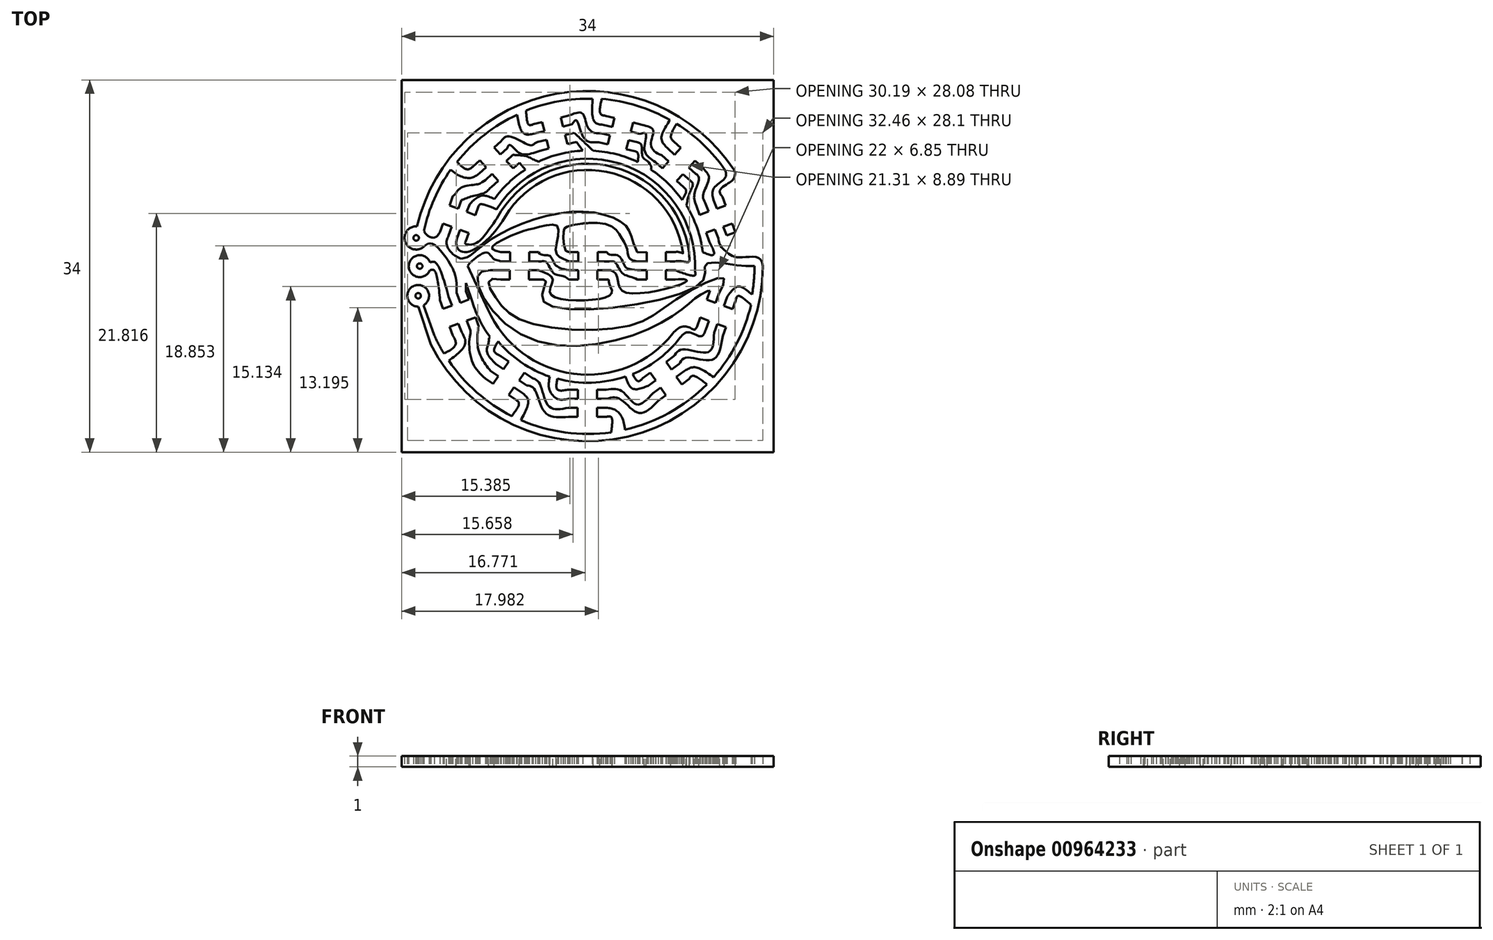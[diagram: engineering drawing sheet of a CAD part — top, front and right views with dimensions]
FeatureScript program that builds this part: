
annotation { "Feature Type Name" : "Feature", "Feature Type Description" : "" }
export const myFeature = defineFeature(function(context is Context, id is Id, definition is map)
    precondition{}
    {
        {
            var Q0;
            Q0=qCreatedBy(makeId("Top.planeOp"),FACE);
            var sketch = newSketch(context, id + "F0", { "sketchPlane" : qUnion([Q0])});
            skLineSegment(sketch, "E0", {"start": v(-17.5, -17.5) * mm, "end": v(17.5, -17.5) * mm});
            skLineSegment(sketch, "E1", {"start": v(17.5, -17.5) * mm, "end": v(17.5, 17.5) * mm});
            skLineSegment(sketch, "E2", {"start": v(17.5, 17.5) * mm, "end": v(-17.5, 17.5) * mm});
            skLineSegment(sketch, "E3", {"start": v(-17.5, 17.5) * mm, "end": v(-17.5, -17.5) * mm});
            skLineSegment(sketch, "E4", {"start": v(7.16, -11.8) * mm, "end": v(6.46, -12.3) * mm});
            skLineSegment(sketch, "E5", {"start": v(5.97, -11.6) * mm, "end": v(6.67, -11.1) * mm});
            skLineSegment(sketch, "E6", {"start": v(6.67, -11.1) * mm, "end": v(7.16, -11.8) * mm});
            skLineSegment(sketch, "E7", {"start": v(6.22, -10.44) * mm, "end": v(5.52, -10.93) * mm});
            skLineSegment(sketch, "E8", {"start": v(5.03, -10.23) * mm, "end": v(5.73, -9.75) * mm});
            skLineSegment(sketch, "E9", {"start": v(5.73, -9.75) * mm, "end": v(6.22, -10.44) * mm});
            skLineSegment(sketch, "E10", {"start": v(8.35, -8.95) * mm, "end": v(7.65, -9.44) * mm});
            skLineSegment(sketch, "E11", {"start": v(7.65, -9.44) * mm, "end": v(7.16, -8.74) * mm});
            skLineSegment(sketch, "E12", {"start": v(7.16, -8.74) * mm, "end": v(7.86, -8.26) * mm});
            skLineSegment(sketch, "E13", {"start": v(9.29, -10.31) * mm, "end": v(8.59, -10.8) * mm});
            skLineSegment(sketch, "E14", {"start": v(8.59, -10.8) * mm, "end": v(8.1, -10.1) * mm});
            skLineSegment(sketch, "E15", {"start": v(8.1, -10.1) * mm, "end": v(8.8, -9.62) * mm});
            skLineSegment(sketch, "E16", {"start": v(-10.85, 3.02) * mm, "end": v(-11.14, 2.22) * mm});
            skLineSegment(sketch, "E17", {"start": v(-11.94, 2.51) * mm, "end": v(-11.65, 3.31) * mm});
            skLineSegment(sketch, "E18", {"start": v(-11.65, 3.31) * mm, "end": v(-10.85, 3.02) * mm});
            skLineSegment(sketch, "E19", {"start": v(-12.4, 3.6) * mm, "end": v(-12.7, 2.8) * mm});
            skLineSegment(sketch, "E20", {"start": v(-13.5, 3.09) * mm, "end": v(-13.2, 3.89) * mm});
            skLineSegment(sketch, "E21", {"start": v(-13.2, 3.89) * mm, "end": v(-12.4, 3.6) * mm});
            skLineSegment(sketch, "E22", {"start": v(-11.51, 6.04) * mm, "end": v(-11.8, 5.24) * mm});
            skLineSegment(sketch, "E23", {"start": v(-11.8, 5.24) * mm, "end": v(-12.6, 5.53) * mm});
            skLineSegment(sketch, "E24", {"start": v(-12.6, 5.53) * mm, "end": v(-12.31, 6.38) * mm});
            skLineSegment(sketch, "E25", {"start": v(-9.96, 5.46) * mm, "end": v(-10.25, 4.66) * mm});
            skLineSegment(sketch, "E26", {"start": v(-10.25, 4.66) * mm, "end": v(-11.05, 4.96) * mm});
            skLineSegment(sketch, "E27", {"start": v(-11.05, 4.96) * mm, "end": v(-10.76, 5.65) * mm});
            skLineSegment(sketch, "E28", {"start": v(1.83, 11.11) * mm, "end": v(1, 11.32) * mm});
            skLineSegment(sketch, "E29", {"start": v(1.21, 12.14) * mm, "end": v(2.04, 11.94) * mm});
            skLineSegment(sketch, "E30", {"start": v(2.04, 11.94) * mm, "end": v(1.83, 11.11) * mm});
            skLineSegment(sketch, "E31", {"start": v(2.24, 12.71) * mm, "end": v(1.42, 12.92) * mm});
            skLineSegment(sketch, "E32", {"start": v(1.63, 13.74) * mm, "end": v(2.45, 13.54) * mm});
            skLineSegment(sketch, "E33", {"start": v(2.45, 13.54) * mm, "end": v(2.24, 12.71) * mm});
            skLineSegment(sketch, "E34", {"start": v(4.77, 12.09) * mm, "end": v(3.94, 12.3) * mm});
            skLineSegment(sketch, "E35", {"start": v(3.94, 12.3) * mm, "end": v(4.15, 13.12) * mm});
            skLineSegment(sketch, "E36", {"start": v(4.15, 13.12) * mm, "end": v(4.97, 12.9) * mm});
            skLineSegment(sketch, "E37", {"start": v(4.36, 10.48) * mm, "end": v(3.53, 10.69) * mm});
            skLineSegment(sketch, "E38", {"start": v(3.53, 10.69) * mm, "end": v(3.74, 11.51) * mm});
            skLineSegment(sketch, "E39", {"start": v(3.74, 11.51) * mm, "end": v(4.56, 11.3) * mm});
            skLineSegment(sketch, "E40", {"start": v(-2.45, 13.58) * mm, "end": v(-1.63, 13.8) * mm});
            skLineSegment(sketch, "E41", {"start": v(-1.42, 12.97) * mm, "end": v(-2.24, 12.76) * mm});
            skLineSegment(sketch, "E42", {"start": v(-2.24, 12.76) * mm, "end": v(-2.45, 13.58) * mm});
            skLineSegment(sketch, "E43", {"start": v(-2.06, 11.98) * mm, "end": v(-1.24, 12.18) * mm});
            skLineSegment(sketch, "E44", {"start": v(-1.03, 11.36) * mm, "end": v(-1.86, 11.15) * mm});
            skLineSegment(sketch, "E45", {"start": v(-1.86, 11.15) * mm, "end": v(-2.06, 11.98) * mm});
            skLineSegment(sketch, "E46", {"start": v(-4.58, 11.35) * mm, "end": v(-3.76, 11.55) * mm});
            skLineSegment(sketch, "E47", {"start": v(-3.76, 11.55) * mm, "end": v(-3.55, 10.73) * mm});
            skLineSegment(sketch, "E48", {"start": v(-3.55, 10.73) * mm, "end": v(-4.38, 10.52) * mm});
            skLineSegment(sketch, "E49", {"start": v(-4.97, 12.96) * mm, "end": v(-4.15, 13.16) * mm});
            skLineSegment(sketch, "E50", {"start": v(-4.15, 13.16) * mm, "end": v(-3.94, 12.34) * mm});
            skLineSegment(sketch, "E51", {"start": v(-3.94, 12.34) * mm, "end": v(-4.77, 12.13) * mm});
            skLineSegment(sketch, "E52", {"start": v(-8.54, 10.84) * mm, "end": v(-7.9, 11.41) * mm});
            skLineSegment(sketch, "E53", {"start": v(-7.34, 10.78) * mm, "end": v(-7.97, 10.21) * mm});
            skLineSegment(sketch, "E54", {"start": v(-7.97, 10.21) * mm, "end": v(-8.54, 10.84) * mm});
            skLineSegment(sketch, "E55", {"start": v(-7.44, 9.6) * mm, "end": v(-6.81, 10.18) * mm});
            skLineSegment(sketch, "E56", {"start": v(-6.22, 9.45) * mm, "end": v(-6.8, 8.94) * mm});
            skLineSegment(sketch, "E57", {"start": v(-6.8, 8.94) * mm, "end": v(-7.44, 9.6) * mm});
            skLineSegment(sketch, "E58", {"start": v(-9.34, 7.87) * mm, "end": v(-8.74, 8.44) * mm});
            skLineSegment(sketch, "E59", {"start": v(-8.74, 8.44) * mm, "end": v(-8.17, 7.8) * mm});
            skLineSegment(sketch, "E60", {"start": v(-8.17, 7.8) * mm, "end": v(-8.8, 7.24) * mm});
            skLineSegment(sketch, "E61", {"start": v(-10.47, 9.1) * mm, "end": v(-9.84, 9.67) * mm});
            skLineSegment(sketch, "E62", {"start": v(-9.84, 9.67) * mm, "end": v(-9.27, 9.04) * mm});
            skLineSegment(sketch, "E63", {"start": v(-9.27, 9.04) * mm, "end": v(-9.9, 8.47) * mm});
            skLineSegment(sketch, "E64", {"start": v(6.84, 8.95) * mm, "end": v(6.2, 9.52) * mm});
            skLineSegment(sketch, "E65", {"start": v(6.77, 10.15) * mm, "end": v(7.4, 9.58) * mm});
            skLineSegment(sketch, "E66", {"start": v(7.4, 9.58) * mm, "end": v(6.84, 8.95) * mm});
            skLineSegment(sketch, "E67", {"start": v(7.95, 10.17) * mm, "end": v(7.32, 10.74) * mm});
            skLineSegment(sketch, "E68", {"start": v(7.89, 11.37) * mm, "end": v(8.52, 10.8) * mm});
            skLineSegment(sketch, "E69", {"start": v(8.52, 10.8) * mm, "end": v(7.95, 10.17) * mm});
            skLineSegment(sketch, "E70", {"start": v(9.88, 8.43) * mm, "end": v(9.25, 9) * mm});
            skLineSegment(sketch, "E71", {"start": v(9.25, 9) * mm, "end": v(9.82, 9.63) * mm});
            skLineSegment(sketch, "E72", {"start": v(9.82, 9.63) * mm, "end": v(10.45, 9.06) * mm});
            skLineSegment(sketch, "E73", {"start": v(8.77, 7.21) * mm, "end": v(8.14, 7.78) * mm});
            skLineSegment(sketch, "E74", {"start": v(8.14, 7.78) * mm, "end": v(8.7, 8.41) * mm});
            skLineSegment(sketch, "E75", {"start": v(8.7, 8.41) * mm, "end": v(9.34, 7.84) * mm});
            skLineSegment(sketch, "E76", {"start": v(10.24, 4.7) * mm, "end": v(9.95, 5.5) * mm});
            skLineSegment(sketch, "E77", {"start": v(10.75, 5.78) * mm, "end": v(11.04, 4.98) * mm});
            skLineSegment(sketch, "E78", {"start": v(11.04, 4.98) * mm, "end": v(10.24, 4.7) * mm});
            skLineSegment(sketch, "E79", {"start": v(11.8, 5.25) * mm, "end": v(11.5, 6.05) * mm});
            skLineSegment(sketch, "E80", {"start": v(12.3, 6.34) * mm, "end": v(12.6, 5.54) * mm});
            skLineSegment(sketch, "E81", {"start": v(12.6, 5.54) * mm, "end": v(11.8, 5.25) * mm});
            skLineSegment(sketch, "E82", {"start": v(12.68, 2.8) * mm, "end": v(12.4, 3.6) * mm});
            skLineSegment(sketch, "E83", {"start": v(12.4, 3.6) * mm, "end": v(13.2, 3.9) * mm});
            skLineSegment(sketch, "E84", {"start": v(13.2, 3.9) * mm, "end": v(13.48, 3.1) * mm});
            skLineSegment(sketch, "E85", {"start": v(13.48, 3.1) * mm, "end": v(12.68, 2.8) * mm});
            skLineSegment(sketch, "E86", {"start": v(11.13, 2.25) * mm, "end": v(10.84, 3.05) * mm});
            skLineSegment(sketch, "E87", {"start": v(10.84, 3.05) * mm, "end": v(11.64, 3.34) * mm});
            skLineSegment(sketch, "E88", {"start": v(11.64, 3.34) * mm, "end": v(11.93, 2.54) * mm});
            skLineSegment(sketch, "E89", {"start": v(12.63, -5.57) * mm, "end": v(12.34, -6.36) * mm});
            skLineSegment(sketch, "E90", {"start": v(11.54, -6.07) * mm, "end": v(11.83, -5.27) * mm});
            skLineSegment(sketch, "E91", {"start": v(11.83, -5.27) * mm, "end": v(12.63, -5.57) * mm});
            skLineSegment(sketch, "E92", {"start": v(11.08, -4.99) * mm, "end": v(10.8, -5.79) * mm});
            skLineSegment(sketch, "E93", {"start": v(10, -5.5) * mm, "end": v(10.28, -4.7) * mm});
            skLineSegment(sketch, "E94", {"start": v(10.28, -4.7) * mm, "end": v(11.08, -4.99) * mm});
            skLineSegment(sketch, "E95", {"start": v(11.97, -2.55) * mm, "end": v(11.68, -3.34) * mm});
            skLineSegment(sketch, "E96", {"start": v(11.68, -3.34) * mm, "end": v(10.88, -3.05) * mm});
            skLineSegment(sketch, "E97", {"start": v(10.88, -3.05) * mm, "end": v(11.17, -2.26) * mm});
            skLineSegment(sketch, "E98", {"start": v(13.52, -3.12) * mm, "end": v(13.23, -3.92) * mm});
            skLineSegment(sketch, "E99", {"start": v(13.23, -3.92) * mm, "end": v(12.43, -3.63) * mm});
            skLineSegment(sketch, "E100", {"start": v(12.43, -3.63) * mm, "end": v(12.72, -2.83) * mm});
            skLineSegment(sketch, "E101", {"start": v(-0.9, -13.78) * mm, "end": v(-1.75, -13.78) * mm});
            skLineSegment(sketch, "E102", {"start": v(-1.75, -12.93) * mm, "end": v(-0.9, -12.93) * mm});
            skLineSegment(sketch, "E103", {"start": v(-0.9, -12.93) * mm, "end": v(-0.9, -13.78) * mm});
            skLineSegment(sketch, "E104", {"start": v(-0.9, -12.12) * mm, "end": v(-1.74, -12.12) * mm});
            skLineSegment(sketch, "E105", {"start": v(-1.74, -11.27) * mm, "end": v(-0.9, -11.27) * mm});
            skLineSegment(sketch, "E106", {"start": v(-0.9, -11.27) * mm, "end": v(-0.9, -12.12) * mm});
            skLineSegment(sketch, "E107", {"start": v(1.7, -12.12) * mm, "end": v(0.86, -12.12) * mm});
            skLineSegment(sketch, "E108", {"start": v(0.86, -12.12) * mm, "end": v(0.86, -11.27) * mm});
            skLineSegment(sketch, "E109", {"start": v(0.86, -11.27) * mm, "end": v(1.7, -11.27) * mm});
            skLineSegment(sketch, "E110", {"start": v(1.7, -13.78) * mm, "end": v(0.85, -13.78) * mm});
            skLineSegment(sketch, "E111", {"start": v(0.85, -13.78) * mm, "end": v(0.85, -12.93) * mm});
            skLineSegment(sketch, "E112", {"start": v(0.85, -12.93) * mm, "end": v(1.7, -12.93) * mm});
            skLineSegment(sketch, "E113", {"start": v(-8.65, -10.76) * mm, "end": v(-9.34, -10.27) * mm});
            skLineSegment(sketch, "E114", {"start": v(-8.85, -9.58) * mm, "end": v(-8.16, -10.07) * mm});
            skLineSegment(sketch, "E115", {"start": v(-8.16, -10.07) * mm, "end": v(-8.65, -10.76) * mm});
            skLineSegment(sketch, "E116", {"start": v(-7.69, -9.41) * mm, "end": v(-8.38, -8.93) * mm});
            skLineSegment(sketch, "E117", {"start": v(-7.9, -8.23) * mm, "end": v(-7.2, -8.72) * mm});
            skLineSegment(sketch, "E118", {"start": v(-7.2, -8.72) * mm, "end": v(-7.69, -9.41) * mm});
            skLineSegment(sketch, "E119", {"start": v(-5.56, -10.9) * mm, "end": v(-6.25, -10.42) * mm});
            skLineSegment(sketch, "E120", {"start": v(-6.25, -10.42) * mm, "end": v(-5.77, -9.72) * mm});
            skLineSegment(sketch, "E121", {"start": v(-5.77, -9.72) * mm, "end": v(-5.07, -10.2) * mm});
            skLineSegment(sketch, "E122", {"start": v(-6.52, -12.25) * mm, "end": v(-7.21, -11.77) * mm});
            skLineSegment(sketch, "E123", {"start": v(-7.21, -11.77) * mm, "end": v(-6.72, -11.07) * mm});
            skLineSegment(sketch, "E124", {"start": v(-6.72, -11.07) * mm, "end": v(-6.03, -11.56) * mm});
            skLineSegment(sketch, "E125", {"start": v(-10.24, -4.7) * mm, "end": v(-9.96, -5.45) * mm});
            skLineSegment(sketch, "E126", {"start": v(-10.75, -5.78) * mm, "end": v(-11.04, -4.98) * mm});
            skLineSegment(sketch, "E127", {"start": v(-11.04, -4.98) * mm, "end": v(-10.24, -4.7) * mm});
            skLineSegment(sketch, "E128", {"start": v(-11.8, -5.25) * mm, "end": v(-11.5, -6.05) * mm});
            skLineSegment(sketch, "E129", {"start": v(-12.3, -6.34) * mm, "end": v(-12.6, -5.54) * mm});
            skLineSegment(sketch, "E130", {"start": v(-12.6, -5.54) * mm, "end": v(-11.8, -5.25) * mm});
            skLineSegment(sketch, "E131", {"start": v(-12.68, -2.8) * mm, "end": v(-12.4, -3.6) * mm});
            skLineSegment(sketch, "E132", {"start": v(-12.4, -3.6) * mm, "end": v(-13.2, -3.9) * mm});
            skLineSegment(sketch, "E133", {"start": v(-13.2, -3.9) * mm, "end": v(-13.48, -3.1) * mm});
            skLineSegment(sketch, "E134", {"start": v(-11.1, -2.3) * mm, "end": v(-10.84, -3.05) * mm});
            skLineSegment(sketch, "E135", {"start": v(-10.84, -3.05) * mm, "end": v(-11.64, -3.34) * mm});
            skLineSegment(sketch, "E136", {"start": v(-11.64, -3.34) * mm, "end": v(-11.96, -2.44) * mm});
            skLineSegment(sketch, "E137", {"start": v(0.9, 1.27) * mm, "end": v(1.76, 1.27) * mm});
            skLineSegment(sketch, "E138", {"start": v(1.76, 0.42) * mm, "end": v(0.9, 0.42) * mm});
            skLineSegment(sketch, "E139", {"start": v(0.9, 0.42) * mm, "end": v(0.9, 1.27) * mm});
            skLineSegment(sketch, "E140", {"start": v(0.9, -0.38) * mm, "end": v(1.75, -0.38) * mm});
            skLineSegment(sketch, "E141", {"start": v(1.75, -1.23) * mm, "end": v(0.9, -1.23) * mm});
            skLineSegment(sketch, "E142", {"start": v(0.9, -1.23) * mm, "end": v(0.9, -0.38) * mm});
            skLineSegment(sketch, "E143", {"start": v(-1.7, -0.38) * mm, "end": v(-0.85, -0.38) * mm});
            skLineSegment(sketch, "E144", {"start": v(-0.85, -0.38) * mm, "end": v(-0.85, -1.23) * mm});
            skLineSegment(sketch, "E145", {"start": v(-0.85, -1.23) * mm, "end": v(-1.7, -1.23) * mm});
            skLineSegment(sketch, "E146", {"start": v(-1.7, 1.27) * mm, "end": v(-0.84, 1.27) * mm});
            skLineSegment(sketch, "E147", {"start": v(-0.84, 1.27) * mm, "end": v(-0.84, 0.42) * mm});
            skLineSegment(sketch, "E148", {"start": v(-0.84, 0.42) * mm, "end": v(-1.7, 0.42) * mm});
            skLineSegment(sketch, "E149", {"start": v(-5.34, 1.27) * mm, "end": v(-4.5, 1.27) * mm});
            skLineSegment(sketch, "E150", {"start": v(-4.5, 0.42) * mm, "end": v(-5.34, 0.42) * mm});
            skLineSegment(sketch, "E151", {"start": v(-5.34, 0.42) * mm, "end": v(-5.34, 1.27) * mm});
            skLineSegment(sketch, "E152", {"start": v(-5.35, -0.38) * mm, "end": v(-4.5, -0.38) * mm});
            skLineSegment(sketch, "E153", {"start": v(-4.5, -1.23) * mm, "end": v(-5.35, -1.23) * mm});
            skLineSegment(sketch, "E154", {"start": v(-5.35, -1.23) * mm, "end": v(-5.35, -0.38) * mm});
            skLineSegment(sketch, "E155", {"start": v(-7.94, -0.38) * mm, "end": v(-7.1, -0.38) * mm});
            skLineSegment(sketch, "E156", {"start": v(-7.1, -0.38) * mm, "end": v(-7.1, -1.23) * mm});
            skLineSegment(sketch, "E157", {"start": v(-7.1, -1.23) * mm, "end": v(-7.95, -1.23) * mm});
            skLineSegment(sketch, "E158", {"start": v(-7.94, 1.27) * mm, "end": v(-7.1, 1.27) * mm});
            skLineSegment(sketch, "E159", {"start": v(-7.1, 1.27) * mm, "end": v(-7.1, 0.42) * mm});
            skLineSegment(sketch, "E160", {"start": v(-7.1, 0.42) * mm, "end": v(-7.94, 0.42) * mm});
            skLineSegment(sketch, "E161", {"start": v(7.16, 1.27) * mm, "end": v(8, 1.27) * mm});
            skLineSegment(sketch, "E162", {"start": v(8, 0.42) * mm, "end": v(7.16, 0.42) * mm});
            skLineSegment(sketch, "E163", {"start": v(7.16, 0.42) * mm, "end": v(7.16, 1.27) * mm});
            skLineSegment(sketch, "E164", {"start": v(7.15, -0.38) * mm, "end": v(8, -0.38) * mm});
            skLineSegment(sketch, "E165", {"start": v(8, -1.23) * mm, "end": v(7.15, -1.23) * mm});
            skLineSegment(sketch, "E166", {"start": v(7.15, -1.23) * mm, "end": v(7.15, -0.38) * mm});
            skLineSegment(sketch, "E167", {"start": v(4.55, -0.38) * mm, "end": v(5.4, -0.38) * mm});
            skLineSegment(sketch, "E168", {"start": v(5.4, -0.38) * mm, "end": v(5.4, -1.23) * mm});
            skLineSegment(sketch, "E169", {"start": v(5.4, -1.23) * mm, "end": v(4.55, -1.23) * mm});
            skLineSegment(sketch, "E170", {"start": v(4.54, 1.24) * mm, "end": v(5.4, 1.27) * mm});
            skLineSegment(sketch, "E171", {"start": v(5.4, 1.27) * mm, "end": v(5.4, 0.42) * mm});
            skLineSegment(sketch, "E172", {"start": v(5.4, 0.42) * mm, "end": v(4.56, 0.42) * mm});
            skFitSpline(sketch, "E173", {"points": [v(-4.5, 1.27) * mm, v(-3.5, 0.96) * mm, v(-3.03, 0.24) * mm, v(-1.7, -0.38) * mm], "startDerivative": vector(2.64, -3.87) * mm, "endDerivative": vector(5.84, -1.05) * mm});
            skFitSpline(sketch, "E174", {"points": [v(-4.5, 0.42) * mm, v(-3.8, 0.38) * mm, v(-3.1, -0.65) * mm, v(-1.7, -1.23) * mm], "startDerivative": vector(2.54, -0.29) * mm, "endDerivative": vector(4.22, -3.88) * mm});
            skFitSpline(sketch, "E175", {"points": [v(1.76, 1.27) * mm, v(2.76, 0.98) * mm, v(3.4, 0) * mm, v(4.55, -0.38) * mm], "startDerivative": vector(2.64, -3.87) * mm, "endDerivative": vector(6.94, -0.97) * mm});
            skFitSpline(sketch, "E176", {"points": [v(1.76, 0.42) * mm, v(2.45, 0.38) * mm, v(3.16, -0.64) * mm, v(4.55, -1.23) * mm], "startDerivative": vector(2.54, -0.29) * mm, "endDerivative": vector(3.98, -2.38) * mm});
            skCircle(sketch, "E177", {"center": v(-15.34, 0) * mm, "radius": 0.25 * mm});
            skArc(sketch, "E178", {"start": v(13.36, 8.8) * mm, "mid": v(-2.8, 15.75) * mm, "end": v(-15.58, 3.64) * mm});
            skArc(sketch, "E179", {"start": v(16, 0) * mm, "mid": v(3.67, -15.57) * mm, "end": v(-14.31, -7.15) * mm});
            skArc(sketch, "E180", {"start": v(-8.32, 5.2) * mm, "mid": v(2.93, 9.37) * mm, "end": v(9.8, -0.47) * mm});
            skArc(sketch, "E181", {"start": v(-8.5, 6.14) * mm, "mid": v(-7.22, 7.61) * mm, "end": v(-5.68, 8.82) * mm});
            skArc(sketch, "E182", {"start": v(-4.48, 9.55) * mm, "mid": v(-2.5, 10.25) * mm, "end": v(-0.44, 10.54) * mm});
            skArc(sketch, "E183", {"start": v(0.5, 10.54) * mm, "mid": v(2.6, 10.23) * mm, "end": v(4.58, 9.5) * mm});
            skArc(sketch, "E184", {"start": v(5.77, 8.82) * mm, "mid": v(7.33, 7.58) * mm, "end": v(8.63, 6.05) * mm});
            skArc(sketch, "E185", {"start": v(9.01, 5.55) * mm, "mid": v(10, 3.5) * mm, "end": v(10.5, 1.27) * mm});
            skArc(sketch, "E186", {"start": v(-14.95, 3.23) * mm, "mid": v(-14, 6.15) * mm, "end": v(-12.5, 8.82) * mm});
            skArc(sketch, "E187", {"start": v(-11.93, 9.5) * mm, "mid": v(-9.43, 12) * mm, "end": v(-6.43, 13.84) * mm});
            skArc(sketch, "E188", {"start": v(-5.62, 14.22) * mm, "mid": v(-2.64, 15.06) * mm, "end": v(0.46, 15.28) * mm});
            skArc(sketch, "E189", {"start": v(1.29, 15.28) * mm, "mid": v(4.51, 14.65) * mm, "end": v(7.53, 13.35) * mm});
            skArc(sketch, "E190", {"start": v(8.11, 13) * mm, "mid": v(10.56, 11.1) * mm, "end": v(12.58, 8.75) * mm});
            skFitSpline(sketch, "E191", {"points": [v(1.63, 13.74) * mm, v(1.18, 13.92) * mm, v(1.29, 15.28) * mm], "startDerivative": vector(-1.46, 0.16) * mm, "endDerivative": vector(0.6, 2.7) * mm});
            skFitSpline(sketch, "E192", {"points": [v(1.42, 12.92) * mm, v(0.64, 13.17) * mm, v(0.46, 15.28) * mm], "startDerivative": vector(-2.38, 0.13) * mm, "endDerivative": vector(0.25, 4.28) * mm});
            skFitSpline(sketch, "E193", {"points": [v(-4.97, 12.96) * mm, v(-5.37, 12.92) * mm, v(-5.62, 14.22) * mm], "startDerivative": vector(-1.25, -0.48) * mm, "endDerivative": vector(-0.15, 2.7) * mm});
            skFitSpline(sketch, "E194", {"points": [v(-4.77, 12.13) * mm, v(-5.84, 12.13) * mm, v(-6.43, 13.84) * mm], "startDerivative": vector(-2.78, -0.66) * mm, "endDerivative": vector(-0.64, 3.88) * mm});
            skFitSpline(sketch, "E195", {"points": [v(7.89, 11.37) * mm, v(7.6, 11.76) * mm, v(8.11, 13) * mm], "startDerivative": vector(-1.05, 0.86) * mm, "endDerivative": vector(1.3, 2.28) * mm});
            skFitSpline(sketch, "E196", {"points": [v(7.32, 10.74) * mm, v(6.74, 11.66) * mm, v(7.53, 13.35) * mm], "startDerivative": vector(-1.92, 1.95) * mm, "endDerivative": vector(2.16, 3.22) * mm});
            skFitSpline(sketch, "E197", {"points": [v(11.5, 6.05) * mm, v(11.5, 7.1) * mm, v(12.57, 8.1) * mm, v(12.58, 8.75) * mm], "startDerivative": vector(-0.86, 3.26) * mm, "endDerivative": vector(-0.7, 2.5) * mm});
            skFitSpline(sketch, "E198", {"points": [v(12.3, 6.34) * mm, v(12.08, 6.94) * mm, v(13.04, 7.7) * mm, v(13.35, 8.03) * mm, v(13.36, 8.8) * mm], "startDerivative": vector(-1.95, 2.73) * mm, "endDerivative": vector(-2.58, 3.05) * mm});
            skFitSpline(sketch, "E199", {"points": [v(-10.47, 9.1) * mm, v(-10.97, 8.84) * mm, v(-11.93, 9.5) * mm], "startDerivative": vector(-1.13, -1.02) * mm, "endDerivative": vector(-1.76, 1.66) * mm});
            skFitSpline(sketch, "E200", {"points": [v(-9.9, 8.47) * mm, v(-10.8, 8.05) * mm, v(-12.5, 8.82) * mm], "startDerivative": vector(-2, -1.6) * mm, "endDerivative": vector(-2.69, 2.72) * mm});
            skArc(sketch, "E201", {"start": v(-14.41, -0.38) * mm, "mid": v(-16.34, 0.02) * mm, "end": v(-14.4, 0.33) * mm});
            skFitSpline(sketch, "E202", {"points": [v(-12.31, 6.38) * mm, v(-11.61, 7.13) * mm, v(-10.14, 7.46) * mm, v(-9.34, 7.87) * mm], "startDerivative": vector(2.35, 1.53) * mm, "endDerivative": vector(4.22, 3) * mm});
            skFitSpline(sketch, "E203", {"points": [v(-11.51, 6.04) * mm, v(-10.56, 6.38) * mm, v(-9.34, 6.74) * mm, v(-8.8, 7.24) * mm], "startDerivative": vector(2.4, 0.9) * mm, "endDerivative": vector(1.63, 1.7) * mm});
            skFitSpline(sketch, "E204", {"points": [v(-7.9, 11.41) * mm, v(-7.29, 11.85) * mm, v(-5.98, 11.37) * mm, v(-5.18, 11.04) * mm, v(-4.58, 11.35) * mm], "startDerivative": vector(2.66, 3.35) * mm, "endDerivative": vector(2.59, 1.34) * mm});
            skFitSpline(sketch, "E205", {"points": [v(-7.34, 10.78) * mm, v(-7.13, 11.08) * mm, v(-6.38, 10.44) * mm, v(-5.7, 10.2) * mm, v(-4.38, 10.52) * mm], "startDerivative": vector(0.96, 2.67) * mm, "endDerivative": vector(4.46, 1.45) * mm});
            skFitSpline(sketch, "E206", {"points": [v(-1.63, 13.8) * mm, v(-0.47, 13.94) * mm, v(0, 12.7) * mm, v(1.21, 12.14) * mm], "startDerivative": vector(4.74, 1.94) * mm, "endDerivative": vector(5.2, 0.66) * mm});
            skFitSpline(sketch, "E207", {"points": [v(-1.42, 12.97) * mm, v(-1.02, 13.32) * mm, v(-0.6, 12.26) * mm, v(0, 11.41) * mm, v(1, 11.32) * mm], "startDerivative": vector(2.61, 4.43) * mm, "endDerivative": vector(4.4, 0.2) * mm});
            skFitSpline(sketch, "E208", {"points": [v(4.97, 12.9) * mm, v(5.97, 12.43) * mm, v(5.78, 11.12) * mm, v(6.77, 10.15) * mm], "startDerivative": vector(3.91, -0.95) * mm, "endDerivative": vector(4.74, -1.03) * mm});
            skFitSpline(sketch, "E209", {"points": [v(4.77, 12.09) * mm, v(5.32, 12.09) * mm, v(5.2, 10.58) * mm, v(6.2, 9.52) * mm], "startDerivative": vector(3.05, 0.85) * mm, "endDerivative": vector(3.66, -2.17) * mm});
            skFitSpline(sketch, "E210", {"points": [v(10.45, 9.06) * mm, v(11.08, 8.13) * mm, v(10.6, 6.74) * mm, v(10.75, 5.78) * mm], "startDerivative": vector(2.43, -3.28) * mm, "endDerivative": vector(2.43, -3.56) * mm});
            skFitSpline(sketch, "E211", {"points": [v(9.88, 8.43) * mm, v(10.16, 7.85) * mm, v(9.8, 6.82) * mm, v(9.95, 5.5) * mm], "startDerivative": vector(2.93, -1.68) * mm, "endDerivative": vector(1.97, -3.76) * mm});
            skFitSpline(sketch, "E212", {"points": [v(-6.81, 10.18) * mm, v(-5.65, 10.06) * mm, v(-4.48, 9.55) * mm], "startDerivative": vector(2, -0.4) * mm, "endDerivative": vector(2.64, -0.83) * mm});
            skFitSpline(sketch, "E213", {"points": [v(-1.24, 12.18) * mm, v(-0.5, 11.5) * mm, v(0.5, 10.54) * mm], "startDerivative": vector(1.55, -1.43) * mm, "endDerivative": vector(1.92, -1.85) * mm});
            skFitSpline(sketch, "E214", {"points": [v(-1.03, 11.36) * mm, v(-0.44, 10.54) * mm], "startDerivative": vector(0.6, -0.82) * mm, "endDerivative": vector(0.6, -0.82) * mm});
            skFitSpline(sketch, "E215", {"points": [v(4.56, 11.3) * mm, v(4.9, 11.08) * mm, v(5.02, 9.99) * mm, v(5.47, 9.6) * mm, v(5.77, 8.82) * mm], "startDerivative": vector(2.08, -0.56) * mm, "endDerivative": vector(-1.82, -2.04) * mm});
            skFitSpline(sketch, "E216", {"points": [v(4.58, 9.5) * mm, v(4.58, 10.34) * mm, v(4.36, 10.48) * mm], "startDerivative": vector(0.2, 1.59) * mm, "endDerivative": vector(-0.73, 0.24) * mm});
            skFitSpline(sketch, "E217", {"points": [v(9.34, 7.84) * mm, v(9.6, 7.53) * mm, v(9.34, 6.73) * mm, v(9.01, 5.55) * mm], "startDerivative": vector(1.53, -1.11) * mm, "endDerivative": vector(-0.61, -2.91) * mm});
            skFitSpline(sketch, "E218", {"points": [v(8.77, 7.21) * mm, v(9, 6.9) * mm, v(8.63, 6.05) * mm], "startDerivative": vector(0.82, -0.66) * mm, "endDerivative": vector(-0.97, -1.59) * mm});
            skFitSpline(sketch, "E219", {"points": [v(-9.96, -5.45) * mm, v(-9.96, -7.68) * mm, v(-8.85, -9.58) * mm], "startDerivative": vector(-0.59, -4.8) * mm, "endDerivative": vector(2.81, -3.35) * mm});
            skFitSpline(sketch, "E220", {"points": [v(-10.75, -5.78) * mm, v(-10.79, -6.54) * mm, v(-10.51, -8.78) * mm, v(-9.34, -10.27) * mm], "startDerivative": vector(1.48, -2.16) * mm, "endDerivative": vector(3.99, -3.62) * mm});
            skFitSpline(sketch, "E221", {"points": [v(-5.07, -10.2) * mm, v(-4.4, -10.72) * mm, v(-3.52, -12.81) * mm, v(-1.75, -12.93) * mm], "startDerivative": vector(3.03, -1.16) * mm, "endDerivative": vector(5.75, 1.17) * mm});
            skFitSpline(sketch, "E222", {"points": [v(-5.56, -10.9) * mm, v(-4.87, -11.2) * mm, v(-3.92, -13.34) * mm, v(-1.75, -13.78) * mm], "startDerivative": vector(3.37, -0.3) * mm, "endDerivative": vector(6.57, 0.36) * mm});
            skFitSpline(sketch, "E223", {"points": [v(1.7, -11.27) * mm, v(3.14, -11.43) * mm, v(4.46, -12.63) * mm, v(5.97, -11.6) * mm], "startDerivative": vector(4.89, 0.68) * mm, "endDerivative": vector(4.53, 4.94) * mm});
            skFitSpline(sketch, "E224", {"points": [v(1.7, -12.12) * mm, v(2.93, -12.12) * mm, v(4.65, -13.4) * mm, v(6.46, -12.3) * mm], "startDerivative": vector(4.41, 1.2) * mm, "endDerivative": vector(5.06, 5.13) * mm});
            skFitSpline(sketch, "E225", {"points": [v(7.86, -8.26) * mm, v(8.69, -7.6) * mm, v(11.03, -7.84) * mm, v(11.54, -6.07) * mm], "startDerivative": vector(2.3, 3.47) * mm, "endDerivative": vector(0.11, 6.8) * mm});
            skFitSpline(sketch, "E226", {"points": [v(8.35, -8.95) * mm, v(9.05, -8.36) * mm, v(11.4, -8.54) * mm, v(12.34, -6.36) * mm], "startDerivative": vector(2.08, 3.44) * mm, "endDerivative": vector(1.17, 7.62) * mm});
            skFitSpline(sketch, "E227", {"points": [v(10.5, 1.27) * mm, v(11.51, 1.05) * mm, v(11.13, 2.25) * mm], "startDerivative": vector(2.79, -1.13) * mm, "endDerivative": vector(-1.48, 3.01) * mm});
            skFitSpline(sketch, "E228", {"points": [v(11.93, 2.54) * mm, v(12.6, 1.37) * mm, v(13.84, 0.8) * mm, v(16, 0) * mm], "startDerivative": vector(0.52, -6.32) * mm, "endDerivative": vector(0.27, -9.23) * mm});
            skFitSpline(sketch, "E229", {"points": [v(8, -0.38) * mm, v(9.8, -0.83) * mm, v(9.8, -0.47) * mm], "startDerivative": vector(3.5, -1.3) * mm, "endDerivative": vector(-0.4, 1.48) * mm});
            skArc(sketch, "E230", {"start": v(15.24, 0) * mm, "mid": v(15.19, -1.3) * mm, "end": v(15.02, -2.59) * mm});
            skArc(sketch, "E231", {"start": v(14.93, -3.54) * mm, "mid": v(13.63, -7.05) * mm, "end": v(11.52, -10.14) * mm});
            skArc(sketch, "E232", {"start": v(10.88, -10.8) * mm, "mid": v(7.44, -13.4) * mm, "end": v(3.4, -14.95) * mm});
            skArc(sketch, "E233", {"start": v(2.15, -15.18) * mm, "mid": v(-2.05, -15.2) * mm, "end": v(-6.1, -14.07) * mm});
            skArc(sketch, "E234", {"start": v(-6.92, -13.7) * mm, "mid": v(-10.12, -11.53) * mm, "end": v(-12.68, -8.64) * mm});
            skArc(sketch, "E235", {"start": v(-13.12, -7.99) * mm, "mid": v(-13.59, -7.18) * mm, "end": v(-14, -6.34) * mm});
            skPoint(sketch, "E236.1.internal.snap0", {"position": v(-13.59, -7.18) * mm});
            skFitSpline(sketch, "E236", {"points": [v(-12.3, -6.34) * mm, v(-12.07, -7.18) * mm, v(-13.12, -7.99) * mm], "startDerivative": vector(1.07, -1.97) * mm, "endDerivative": vector(-2.58, -1.36) * mm});
            skFitSpline(sketch, "E237", {"points": [v(-11.5, -6.05) * mm, v(-11.18, -7.1) * mm, v(-12.68, -8.64) * mm], "startDerivative": vector(1.48, -2.5) * mm, "endDerivative": vector(-3.56, -2.68) * mm});
            skFitSpline(sketch, "E238", {"points": [v(-6.52, -12.25) * mm, v(-6.27, -12.53) * mm, v(-6.92, -13.7) * mm], "startDerivative": vector(1, -0.63) * mm, "endDerivative": vector(-1.55, -2.1) * mm});
            skFitSpline(sketch, "E239", {"points": [v(-6.03, -11.56) * mm, v(-5.43, -12.25) * mm, v(-6.1, -14.07) * mm], "startDerivative": vector(1.98, -1.43) * mm, "endDerivative": vector(-1.89, -3.46) * mm});
            skFitSpline(sketch, "E240", {"points": [v(1.7, -13.78) * mm, v(2.15, -13.78) * mm, v(2.15, -15.18) * mm], "startDerivative": vector(1.48, 0.4) * mm, "endDerivative": vector(-0.4, -2.9) * mm});
            skFitSpline(sketch, "E241", {"points": [v(1.7, -12.93) * mm, v(2.75, -13.3) * mm, v(3.4, -14.95) * mm], "startDerivative": vector(2.76, -0.33) * mm, "endDerivative": vector(0.2, -3.71) * mm});
            skFitSpline(sketch, "E242", {"points": [v(9.29, -10.31) * mm, v(9.59, -10) * mm, v(10.88, -10.8) * mm], "startDerivative": vector(0.68, 1.24) * mm, "endDerivative": vector(2.34, -1.9) * mm});
            skFitSpline(sketch, "E243", {"points": [v(8.8, -9.62) * mm, v(9.75, -9.24) * mm, v(11.52, -10.14) * mm], "startDerivative": vector(2.12, 1.42) * mm, "endDerivative": vector(3.25, -2.26) * mm});
            skFitSpline(sketch, "E244", {"points": [v(13.52, -3.12) * mm, v(13.74, -2.73) * mm, v(14.93, -3.54) * mm], "startDerivative": vector(0.39, 1.52) * mm, "endDerivative": vector(2.25, -2.02) * mm});
            skFitSpline(sketch, "E245", {"points": [v(12.72, -2.83) * mm, v(13.74, -1.87) * mm, v(15.02, -2.59) * mm], "startDerivative": vector(1.95, 2.82) * mm, "endDerivative": vector(2.85, -2.31) * mm});
            skFitSpline(sketch, "E246", {"points": [v(15.24, 0) * mm, v(14.45, 0) * mm, v(10.82, 0.18) * mm, v(10.45, -1.44) * mm, v(-3.97, -3.3) * mm, v(-3.82, -1.37) * mm, v(-4.5, -1.23) * mm], "startDerivative": vector(-5.24, 2.42) * mm, "endDerivative": vector(-11.7, -0.76) * mm});
            skFitSpline(sketch, "E247", {"points": [v(8, -1.23) * mm, v(8.93, -1.23) * mm, v(9.05, -1.37) * mm, v(3.4, -2.4) * mm, v(2.7, -1) * mm, v(1.75, -0.38) * mm], "startDerivative": vector(6.97, 0.55) * mm, "endDerivative": vector(-8.34, -1.85) * mm});
            skFitSpline(sketch, "E248", {"points": [v(1.75, -1.23) * mm, v(1.96, -1.5) * mm, v(2.2, -2.47) * mm, v(-0.27, -3.12) * mm, v(-3.44, -2.45) * mm, v(-3.19, -1.23) * mm, v(-4.5, -0.38) * mm], "startDerivative": vector(5.65, 7.44) * mm, "endDerivative": vector(-11.9, 3.97) * mm});
            skFitSpline(sketch, "E249", {"points": [v(-14.4, 0.33) * mm, v(-13.9, 0.33) * mm, v(-12.68, -2.8) * mm], "startDerivative": vector(1.77, 0.6) * mm, "endDerivative": vector(1.66, -5.9) * mm});
            skFitSpline(sketch, "E250", {"points": [v(-14.41, -0.38) * mm, v(-14.02, -0.38) * mm, v(-13.48, -3.1) * mm], "startDerivative": vector(1.53, 0.51) * mm, "endDerivative": vector(0.49, -5.1) * mm});
            skFitSpline(sketch, "E251", {"points": [v(11.17, -2.26) * mm, v(10.77, -2.33) * mm, v(9.31, -3.37) * mm, v(5.06, -5.97) * mm, v(-6.09, -6.24) * mm, v(-10.03, -0.86) * mm, v(-7.94, -0.38) * mm], "startDerivative": vector(10.42, 9.09) * mm, "endDerivative": vector(22.58, -1.13) * mm});
            skFitSpline(sketch, "E252", {"points": [v(11.97, -2.55) * mm, v(12.39, -1.08) * mm, v(7.88, -3.18) * mm, v(3.8, -5.45) * mm, v(-5.65, -5.1) * mm, v(-8.28, -3.05) * mm, v(-9.03, -1.4) * mm, v(-7.95, -1.23) * mm], "startDerivative": vector(11.15, 20.44) * mm, "endDerivative": vector(20.24, -6.25) * mm});
            skFitSpline(sketch, "E253", {"points": [v(-10.76, 5.65) * mm, v(-9.81, 6.4) * mm, v(-8.5, 6.14) * mm], "startDerivative": vector(0.62, 1.08) * mm, "endDerivative": vector(3.76, -1.4) * mm});
            skFitSpline(sketch, "E254", {"points": [v(-9.96, 5.46) * mm, v(-9.77, 5.65) * mm, v(-8.96, 5.46) * mm, v(-8.32, 5.2) * mm], "startDerivative": vector(0.36, 1.58) * mm, "endDerivative": vector(1.62, -0.6) * mm});
            skArc(sketch, "E255", {"start": v(9.27, 1.25) * mm, "mid": v(1.64, 9.2) * mm, "end": v(-8.27, 4.37) * mm});
            skArc(sketch, "E256", {"start": v(8.7, 1.27) * mm, "mid": v(1.73, 8.62) * mm, "end": v(-7.53, 4.53) * mm});
            skFitSpline(sketch, "E257", {"points": [v(8.7, 1.27) * mm, v(8.7, 1.17) * mm, v(8.39, 1.27) * mm, v(8, 1.27) * mm], "startDerivative": vector(0.26, -1.93) * mm, "endDerivative": vector(-1.2, -0.41) * mm});
            skFitSpline(sketch, "E258", {"points": [v(8, 0.42) * mm, v(8.7, 0.42) * mm, v(9.27, 0.42) * mm, v(9.27, 1.25) * mm], "startDerivative": vector(2.4, 0.62) * mm, "endDerivative": vector(0.25, 2.96) * mm});
            skFitSpline(sketch, "E259", {"points": [v(-11.14, 2.22) * mm, v(-10.56, 1.98) * mm, v(-8.27, 4.37) * mm], "startDerivative": vector(-2.23, -2) * mm, "endDerivative": vector(4.2, 5.67) * mm});
            skFitSpline(sketch, "E260", {"points": [v(-11.94, 2.51) * mm, v(-11.94, 1.76) * mm, v(-11.14, 1.27) * mm, v(-7.53, 4.53) * mm], "startDerivative": vector(-0.67, -3.4) * mm, "endDerivative": vector(5.57, 9.92) * mm});
            skFitSpline(sketch, "E261", {"points": [v(4.54, 1.24) * mm, v(3.45, 3.72) * mm, v(-0.65, 4.98) * mm, v(-7.99, 2.94) * mm, v(-10.62, 1.06) * mm, v(-11.54, 0.67) * mm], "startDerivative": vector(-9.7, 21.52) * mm, "endDerivative": vector(-16.59, -4.42) * mm});
            skFitSpline(sketch, "E262", {"points": [v(4.56, 0.42) * mm, v(3.74, 0.84) * mm, v(3.62, 1.52) * mm, v(3.16, 2.51) * mm, v(1.9, 3.77) * mm, v(-1.84, 3.61) * mm, v(-2.2, 3) * mm, v(-1.7, 1.27) * mm], "startDerivative": vector(-11.9, 0.59) * mm, "endDerivative": vector(9.26, 3.22) * mm});
            skFitSpline(sketch, "E263", {"points": [v(-1.7, 0.42) * mm, v(-2.34, 0.73) * mm, v(-2.9, 1.4) * mm, v(-2.74, 3.62) * mm, v(-4.63, 3.53) * mm, v(-6.4, 3.01) * mm, v(-8.75, 1.67) * mm, v(-7.94, 1.27) * mm], "startDerivative": vector(-5.6, 3.4) * mm, "endDerivative": vector(11.59, -2.8) * mm});
            skFitSpline(sketch, "E264", {"points": [v(-7.94, 0.42) * mm, v(-8.55, 0.63) * mm, v(-9.22, 1.24) * mm, v(-10.6, 0.42) * mm, v(-10.94, 0) * mm], "startDerivative": vector(-2.78, 1.7) * mm, "endDerivative": vector(-1.02, -3.18) * mm});
            skArc(sketch, "E265", {"start": v(7.78, -6.15) * mm, "mid": v(-1.29, -9.84) * mm, "end": v(-9.1, -3.95) * mm});
            skArc(sketch, "E266", {"start": v(8.2, -6.84) * mm, "mid": v(6.34, -8.6) * mm, "end": v(4.1, -9.86) * mm});
            skArc(sketch, "E267", {"start": v(3.46, -10.07) * mm, "mid": v(0.36, -10.64) * mm, "end": v(-2.76, -10.29) * mm});
            skArc(sketch, "E268", {"start": v(-3.46, -10.1) * mm, "mid": v(-6.03, -8.8) * mm, "end": v(-8.16, -6.88) * mm});
            skArc(sketch, "E269", {"start": v(-8.93, -6.47) * mm, "mid": v(-9.85, -4.96) * mm, "end": v(-10.51, -3.32) * mm});
            skFitSpline(sketch, "E270", {"points": [v(10.8, -5.79) * mm, v(10.34, -6.41) * mm, v(9.2, -6.04) * mm, v(8.2, -6.84) * mm], "startDerivative": vector(-1.16, -3.18) * mm, "endDerivative": vector(-2.46, -3.34) * mm});
            skFitSpline(sketch, "E271", {"points": [v(7.78, -6.15) * mm, v(8.97, -5.5) * mm, v(9.76, -5.79) * mm, v(10, -5.5) * mm], "startDerivative": vector(2.32, 2.8) * mm, "endDerivative": vector(0.74, 1.85) * mm});
            skFitSpline(sketch, "E272", {"points": [v(5.03, -10.23) * mm, v(4.63, -10.52) * mm, v(4.1, -9.86) * mm], "startDerivative": vector(-0.93, -1.04) * mm, "endDerivative": vector(-0.92, 1.67) * mm});
            skFitSpline(sketch, "E273", {"points": [v(5.52, -10.93) * mm, v(4.1, -11.2) * mm, v(3.46, -10.07) * mm], "startDerivative": vector(-3.11, -1.23) * mm, "endDerivative": vector(-1, 2.98) * mm});
            skFitSpline(sketch, "E274", {"points": [v(-1.74, -11.27) * mm, v(-2.76, -11.27) * mm, v(-2.76, -10.29) * mm], "startDerivative": vector(-2.53, -0.5) * mm, "endDerivative": vector(0.5, 2.49) * mm});
            skFitSpline(sketch, "E275", {"points": [v(-1.74, -12.12) * mm, v(-2.76, -12.12) * mm, v(-3.49, -11.27) * mm, v(-3.46, -10.1) * mm], "startDerivative": vector(-3.3, -0.6) * mm, "endDerivative": vector(0.6, 3.49) * mm});
            skFitSpline(sketch, "E276", {"points": [v(-7.9, -8.23) * mm, v(-8.53, -7.76) * mm, v(-8.16, -6.88) * mm], "startDerivative": vector(-1.8, 0.81) * mm, "endDerivative": vector(1.22, 1.88) * mm});
            skFitSpline(sketch, "E277", {"points": [v(-8.38, -8.93) * mm, v(-9.2, -7.81) * mm, v(-9.06, -7.06) * mm, v(-8.93, -6.47) * mm], "startDerivative": vector(-2.79, 2.9) * mm, "endDerivative": vector(1.25, 2.47) * mm});
            skLineSegment(sketch, "E278", {"start": v(-9.1, -3.95) * mm, "end": v(-10.94, 0) * mm});
            skFitSpline(sketch, "E279", {"points": [v(-11.54, 0.67) * mm, v(-12.4, 1.18) * mm, v(-12.88, 2.07) * mm, v(-12.7, 2.8) * mm], "startDerivative": vector(-3.04, 1.31) * mm, "endDerivative": vector(1.1, 2.4) * mm});
            skLineSegment(sketch, "E280", {"start": v(-10.51, -3.32) * mm, "end": v(-11.1, -1.55) * mm});
            skCircle(sketch, "E281", {"center": v(-15.66, 2.58) * mm, "radius": 0.25 * mm});
            skArc(sketch, "E282", {"start": v(-15.58, 3.64) * mm, "mid": v(-16.67, 2.24) * mm, "end": v(-14.95, 1.78) * mm});
            skFitSpline(sketch, "E283", {"points": [v(-14.95, 3.23) * mm, v(-14.73, 2.88) * mm, v(-14.03, 2.6) * mm, v(-13.5, 3.09) * mm], "startDerivative": vector(0.56, -1.29) * mm, "endDerivative": vector(1.3, 1.87) * mm});
            skFitSpline(sketch, "E284", {"points": [v(-11.96, -2.44) * mm, v(-11.96, -1.52) * mm, v(-12.2, -0.54) * mm, v(-12.7, 0.44) * mm, v(-14.24, 2.07) * mm, v(-14.95, 1.78) * mm], "startDerivative": vector(-0.83, 7.28) * mm, "endDerivative": vector(-3.94, -3.18) * mm});
            skCircle(sketch, "E285", {"center": v(-15.48, -2.7) * mm, "radius": 0.25 * mm});
            skArc(sketch, "E286", {"start": v(-14.98, -3.57) * mm, "mid": v(-15.73, -1.75) * mm, "end": v(-15.48, -3.7) * mm});
            skLineSegment(sketch, "E287", {"start": v(-14, -6.34) * mm, "end": v(-14.98, -3.57) * mm});
            skLineSegment(sketch, "E288", {"start": v(-14.31, -7.15) * mm, "end": v(-15.48, -3.7) * mm});
            skPoint(sketch, "E289", {"position": v(-6.51, 9.2) * mm});
            skLineSegment(sketch, "E290", {"start": v(-6.22, 9.45) * mm, "end": v(-5.68, 8.82) * mm});
            skLineSegment(sketch, "E291", {"start": v(-11.1, -2.3) * mm, "end": v(-11.1, -1.55) * mm});
            skLineSegment(sketch, "E292.bottom", {"start": v(17, 17) * mm, "end": v(-17, 17) * mm});
            skLineSegment(sketch, "E292.top", {"start": v(17, -17) * mm, "end": v(-17, -17) * mm});
            skLineSegment(sketch, "E292.left", {"start": v(17, 17) * mm, "end": v(17, -17) * mm});
            skLineSegment(sketch, "E292.right", {"start": v(-17, 17) * mm, "end": v(-17, -17) * mm});
            skLineSegment(sketch, "E293", {"start": v(-13.2, 3.89) * mm, "end": v(-12.6, 5.53) * mm});
            skLineSegment(sketch, "E294", {"start": v(-12.6, 5.53) * mm, "end": v(-10.25, 4.66) * mm});
            skLineSegment(sketch, "E295", {"start": v(-10.25, 4.66) * mm, "end": v(-10.85, 3.02) * mm});
            skLineSegment(sketch, "E296", {"start": v(-10.85, 3.02) * mm, "end": v(-13.2, 3.89) * mm});
            skLineSegment(sketch, "E297", {"start": v(-8.17, 7.8) * mm, "end": v(-6.8, 8.94) * mm});
            skLineSegment(sketch, "E298", {"start": v(-6.82, 9) * mm, "end": v(-8.54, 10.84) * mm});
            skLineSegment(sketch, "E299", {"start": v(-8.54, 10.84) * mm, "end": v(-9.84, 9.67) * mm});
            skLineSegment(sketch, "E300", {"start": v(-9.84, 9.67) * mm, "end": v(-8.17, 7.8) * mm});
            skLineSegment(sketch, "E301", {"start": v(-4.15, 13.16) * mm, "end": v(-2.45, 13.58) * mm});
            skLineSegment(sketch, "E302", {"start": v(-2.42, 13.6) * mm, "end": v(-1.86, 11.15) * mm});
            skLineSegment(sketch, "E303", {"start": v(-1.8, 11.18) * mm, "end": v(-3.55, 10.73) * mm});
            skLineSegment(sketch, "E304", {"start": v(-3.55, 10.74) * mm, "end": v(-4.15, 13.16) * mm});
            skLineSegment(sketch, "E305", {"start": v(3.53, 10.69) * mm, "end": v(1.83, 11.11) * mm});
            skLineSegment(sketch, "E306", {"start": v(1.86, 11.13) * mm, "end": v(2.45, 13.54) * mm});
            skLineSegment(sketch, "E307", {"start": v(2.45, 13.54) * mm, "end": v(4.15, 13.12) * mm});
            skLineSegment(sketch, "E308", {"start": v(4.15, 13.12) * mm, "end": v(3.53, 10.69) * mm});
            skLineSegment(sketch, "E309", {"start": v(8.14, 7.78) * mm, "end": v(6.84, 8.95) * mm});
            skLineSegment(sketch, "E310", {"start": v(6.84, 8.95) * mm, "end": v(8.52, 10.8) * mm});
            skLineSegment(sketch, "E311", {"start": v(8.52, 10.8) * mm, "end": v(9.82, 9.63) * mm});
            skLineSegment(sketch, "E312", {"start": v(9.82, 9.63) * mm, "end": v(8.14, 7.78) * mm});
            skLineSegment(sketch, "E313", {"start": v(10.24, 4.7) * mm, "end": v(12.6, 5.54) * mm});
            skLineSegment(sketch, "E314", {"start": v(12.6, 5.54) * mm, "end": v(13.2, 3.9) * mm});
            skLineSegment(sketch, "E315", {"start": v(13.2, 3.9) * mm, "end": v(10.84, 3.05) * mm});
            skLineSegment(sketch, "E316", {"start": v(10.84, 3.05) * mm, "end": v(10.24, 4.7) * mm});
            skLineSegment(sketch, "E317", {"start": v(-7.1, 1.27) * mm, "end": v(-5.34, 1.27) * mm});
            skLineSegment(sketch, "E318", {"start": v(-5.34, 1.27) * mm, "end": v(-5.35, -1.23) * mm});
            skLineSegment(sketch, "E319", {"start": v(-5.35, -1.23) * mm, "end": v(-7.1, -1.23) * mm});
            skLineSegment(sketch, "E320", {"start": v(-7.1, -1.23) * mm, "end": v(-7.1, 1.27) * mm});
            skLineSegment(sketch, "E321", {"start": v(0.9, -1.23) * mm, "end": v(-0.85, -1.23) * mm});
            skLineSegment(sketch, "E322", {"start": v(-0.85, -1.23) * mm, "end": v(-0.84, 1.27) * mm});
            skLineSegment(sketch, "E323", {"start": v(-0.84, 1.27) * mm, "end": v(0.9, 1.27) * mm});
            skLineSegment(sketch, "E324", {"start": v(0.9, 1.27) * mm, "end": v(0.9, -1.23) * mm});
            skLineSegment(sketch, "E325", {"start": v(7.15, -1.23) * mm, "end": v(5.4, -1.23) * mm});
            skLineSegment(sketch, "E326", {"start": v(5.4, -1.23) * mm, "end": v(5.4, 1.27) * mm});
            skLineSegment(sketch, "E327", {"start": v(5.4, 1.27) * mm, "end": v(7.16, 1.27) * mm});
            skLineSegment(sketch, "E328", {"start": v(7.16, 1.27) * mm, "end": v(7.15, -1.23) * mm});
            skLineSegment(sketch, "E329", {"start": v(-12.6, -5.54) * mm, "end": v(-13.2, -3.9) * mm});
            skLineSegment(sketch, "E330", {"start": v(-13.2, -3.9) * mm, "end": v(-10.84, -3.05) * mm});
            skLineSegment(sketch, "E331", {"start": v(-10.84, -3.05) * mm, "end": v(-10.24, -4.7) * mm});
            skLineSegment(sketch, "E332", {"start": v(-10.24, -4.7) * mm, "end": v(-12.6, -5.54) * mm});
            skLineSegment(sketch, "E333", {"start": v(-7.21, -11.77) * mm, "end": v(-8.65, -10.76) * mm});
            skLineSegment(sketch, "E334", {"start": v(-8.65, -10.76) * mm, "end": v(-7.2, -8.72) * mm});
            skLineSegment(sketch, "E335", {"start": v(-7.2, -8.72) * mm, "end": v(-5.77, -9.72) * mm});
            skLineSegment(sketch, "E336", {"start": v(-5.77, -9.72) * mm, "end": v(-7.21, -11.77) * mm});
            skLineSegment(sketch, "E337", {"start": v(0.85, -13.78) * mm, "end": v(-0.9, -13.78) * mm});
            skLineSegment(sketch, "E338", {"start": v(-0.9, -13.78) * mm, "end": v(-0.9, -11.27) * mm});
            skLineSegment(sketch, "E339", {"start": v(-0.9, -11.27) * mm, "end": v(0.86, -11.27) * mm});
            skLineSegment(sketch, "E340", {"start": v(0.86, -11.27) * mm, "end": v(0.85, -13.78) * mm});
            skLineSegment(sketch, "E341", {"start": v(7.16, -11.8) * mm, "end": v(8.59, -10.8) * mm});
            skLineSegment(sketch, "E342", {"start": v(8.59, -10.8) * mm, "end": v(7.16, -8.74) * mm});
            skLineSegment(sketch, "E343", {"start": v(7.16, -8.74) * mm, "end": v(5.73, -9.75) * mm});
            skLineSegment(sketch, "E344", {"start": v(5.73, -9.75) * mm, "end": v(7.16, -11.8) * mm});
            skLineSegment(sketch, "E345", {"start": v(12.63, -5.57) * mm, "end": v(13.23, -3.92) * mm});
            skLineSegment(sketch, "E346", {"start": v(13.23, -3.92) * mm, "end": v(10.88, -3.05) * mm});
            skLineSegment(sketch, "E347", {"start": v(10.88, -3.05) * mm, "end": v(10.28, -4.7) * mm});
            skLineSegment(sketch, "E348", {"start": v(10.28, -4.7) * mm, "end": v(12.63, -5.57) * mm});
            skSolve(sketch);
        }
        {
            var Q0;
            Q0=makeQuery(id+"F0.imprint","IMPRINT",FACE,{"disambiguationData":[TD([[makeQuery(id+"F0.imprint","IMPRINT",EDGE,{"derivedFrom":sQuery(id+"F0.wireOp",EDGE,"E80")}),1.0]])]});
            var Q1;
            Q1=makeQuery(id+"F0.imprint","IMPRINT",FACE,{"disambiguationData":[TD([[makeQuery(id+"F0.imprint","IMPRINT",EDGE,{"derivedFrom":sQuery(id+"F0.wireOp",EDGE,"E20")}),1.0]])]});
            var Q2;
            {var subQ4=sQuery(id+"F0.wireOp",EDGE,"E54");Q2=makeQuery(id+"F0.imprint","IMPRINT",FACE,{"disambiguationData":[TD([[makeQuery(id+"F0.imprint","IMPRINT",EDGE,{"derivedFrom":subQ4}),1.0]])]});}
            var Q3;
            {var subQ7=sQuery(id+"F0.wireOp",EDGE,"E44");Q3=makeQuery(id+"F0.imprint","IMPRINT",FACE,{"disambiguationData":[TD([[makeQuery(id+"F0.imprint","IMPRINT",EDGE,{"derivedFrom":subQ7}),1.0]])]});}
            var Q4;
            {var subQ2=sQuery(id+"F0.wireOp",EDGE,"E42");Q4=makeQuery(id+"F0.imprint","IMPRINT",FACE,{"disambiguationData":[TD([[makeQuery(id+"F0.imprint","IMPRINT",EDGE,{"derivedFrom":subQ2}),1.0]])]});}
            var Q5;
            Q5=makeQuery(id+"F0.imprint","IMPRINT",FACE,{"disambiguationData":[TD([[makeQuery(id+"F0.imprint","IMPRINT",EDGE,{"derivedFrom":sQuery(id+"F0.wireOp",EDGE,"E29")}),1.0]])]});
            var Q6;
            Q6=makeQuery(id+"F0.imprint","IMPRINT",FACE,{"disambiguationData":[TD([[makeQuery(id+"F0.imprint","IMPRINT",EDGE,{"derivedFrom":sQuery(id+"F0.wireOp",EDGE,"E28")}),1.0]])]});
            var Q7;
            Q7=makeQuery(id+"F0.imprint","IMPRINT",FACE,{"disambiguationData":[TD([[makeQuery(id+"F0.imprint","IMPRINT",EDGE,{"derivedFrom":sQuery(id+"F0.wireOp",EDGE,"E17")}),1.0]])]});
            var Q8;
            Q8=makeQuery(id+"F0.imprint","IMPRINT",FACE,{"disambiguationData":[TD([[makeQuery(id+"F0.imprint","IMPRINT",EDGE,{"derivedFrom":sQuery(id+"F0.wireOp",EDGE,"E22")}),1.0]])]});
            var Q9;
            Q9=makeQuery(id+"F0.imprint","IMPRINT",FACE,{"disambiguationData":[TD([[makeQuery(id+"F0.imprint","IMPRINT",EDGE,{"derivedFrom":sQuery(id+"F0.wireOp",EDGE,"E16")}),1.0]])]});
            var Q10;
            Q10=makeQuery(id+"F0.imprint","IMPRINT",FACE,{"disambiguationData":[TD([[makeQuery(id+"F0.imprint","IMPRINT",EDGE,{"derivedFrom":sQuery(id+"F0.wireOp",EDGE,"E93")}),1.0]])]});
            var Q11;
            Q11=makeQuery(id+"F0.imprint","IMPRINT",FACE,{"disambiguationData":[TD([[makeQuery(id+"F0.imprint","IMPRINT",EDGE,{"derivedFrom":sQuery(id+"F0.wireOp",EDGE,"E141")}),1.0]])]});
            var Q12;
            Q12=makeQuery(id+"F0.imprint","IMPRINT",FACE,{"disambiguationData":[TD([[makeQuery(id+"F0.imprint","IMPRINT",EDGE,{"derivedFrom":sQuery(id+"F0.wireOp",EDGE,"E143")}),1.0]])]});
            var Q13;
            Q13=makeQuery(id+"F0.imprint","IMPRINT",FACE,{"disambiguationData":[TD([[makeQuery(id+"F0.imprint","IMPRINT",EDGE,{"derivedFrom":sQuery(id+"F0.wireOp",EDGE,"E137")}),1.0]])]});
            var Q14;
            Q14=makeQuery(id+"F0.imprint","IMPRINT",FACE,{"disambiguationData":[TD([[makeQuery(id+"F0.imprint","IMPRINT",EDGE,{"derivedFrom":sQuery(id+"F0.wireOp",EDGE,"E138")}),1.0]])]});
            var Q15;
            Q15=makeQuery(id+"F0.imprint","IMPRINT",FACE,{"disambiguationData":[TD([[makeQuery(id+"F0.imprint","IMPRINT",EDGE,{"derivedFrom":sQuery(id+"F0.wireOp",EDGE,"E95")}),1.0]])]});
            var Q16;
            Q16=makeQuery(id+"F0.imprint","IMPRINT",FACE,{"disambiguationData":[TD([[makeQuery(id+"F0.imprint","IMPRINT",EDGE,{"derivedFrom":sQuery(id+"F0.wireOp",EDGE,"E10")}),1.0]])]});
            var Q17;
            Q17=makeQuery(id+"F0.imprint","IMPRINT",FACE,{"disambiguationData":[TD([[makeQuery(id+"F0.imprint","IMPRINT",EDGE,{"derivedFrom":sQuery(id+"F0.wireOp",EDGE,"E5")}),1.0]])]});
            var Q18;
            Q18=makeQuery(id+"F0.imprint","IMPRINT",FACE,{"disambiguationData":[TD([[makeQuery(id+"F0.imprint","IMPRINT",EDGE,{"derivedFrom":sQuery(id+"F0.wireOp",EDGE,"E4")}),1.0]])]});
            var Q19;
            Q19=makeQuery(id+"F0.imprint","IMPRINT",FACE,{"disambiguationData":[TD([[makeQuery(id+"F0.imprint","IMPRINT",EDGE,{"derivedFrom":sQuery(id+"F0.wireOp",EDGE,"E101")}),1.0]])]});
            var Q20;
            Q20=makeQuery(id+"F0.imprint","IMPRINT",FACE,{"disambiguationData":[TD([[makeQuery(id+"F0.imprint","IMPRINT",EDGE,{"derivedFrom":sQuery(id+"F0.wireOp",EDGE,"E113")}),1.0]])]});
            var Q21;
            Q21=makeQuery(id+"F0.imprint","IMPRINT",FACE,{"disambiguationData":[TD([[makeQuery(id+"F0.imprint","IMPRINT",EDGE,{"derivedFrom":sQuery(id+"F0.wireOp",EDGE,"E114")}),1.0]])]});
            var Q22;
            Q22=makeQuery(id+"F0.imprint","IMPRINT",FACE,{"disambiguationData":[TD([[makeQuery(id+"F0.imprint","IMPRINT",EDGE,{"derivedFrom":sQuery(id+"F0.wireOp",EDGE,"E102")}),1.0]])]});
            var Q23;
            Q23=makeQuery(id+"F0.imprint","IMPRINT",FACE,{"disambiguationData":[TD([[makeQuery(id+"F0.imprint","IMPRINT",EDGE,{"derivedFrom":sQuery(id+"F0.wireOp",EDGE,"E8")}),1.0]])]});
            var Q24;
            Q24=makeQuery(id+"F0.imprint","IMPRINT",FACE,{"disambiguationData":[TD([[makeQuery(id+"F0.imprint","IMPRINT",EDGE,{"derivedFrom":sQuery(id+"F0.wireOp",EDGE,"E70")}),1.0]])]});
            var Q25;
            Q25=makeQuery(id+"F0.imprint","IMPRINT",FACE,{"disambiguationData":[TD([[makeQuery(id+"F0.imprint","IMPRINT",EDGE,{"derivedFrom":sQuery(id+"F0.wireOp",EDGE,"E68")}),1.0]])]});
            var Q26;
            Q26=makeQuery(id+"F0.imprint","IMPRINT",FACE,{"disambiguationData":[TD([[makeQuery(id+"F0.imprint","IMPRINT",EDGE,{"derivedFrom":sQuery(id+"F0.wireOp",EDGE,"E32")}),1.0]])]});
            var Q27;
            Q27=makeQuery(id+"F0.imprint","IMPRINT",FACE,{"disambiguationData":[TD([[makeQuery(id+"F0.imprint","IMPRINT",EDGE,{"derivedFrom":sQuery(id+"F0.wireOp",EDGE,"E34")}),1.0]])]});
            var Q28;
            {var subQ5=sQuery(id+"F0.wireOp",EDGE,"E69");Q28=makeQuery(id+"F0.imprint","IMPRINT",FACE,{"disambiguationData":[TD([[makeQuery(id+"F0.imprint","IMPRINT",EDGE,{"derivedFrom":subQ5}),1.0]])]});}
            var Q29;
            {var subQ5=sQuery(id+"F0.wireOp",EDGE,"E81");Q29=makeQuery(id+"F0.imprint","IMPRINT",FACE,{"disambiguationData":[TD([[makeQuery(id+"F0.imprint","IMPRINT",EDGE,{"derivedFrom":subQ5}),1.0]])]});}
            var Q30;
            {var subQ5=sQuery(id+"F0.wireOp",EDGE,"E94");Q30=makeQuery(id+"F0.imprint","IMPRINT",FACE,{"disambiguationData":[TD([[makeQuery(id+"F0.imprint","IMPRINT",EDGE,{"derivedFrom":subQ5}),1.0]])]});}
            var Q31;
            {var subQ8=sQuery(id+"F0.wireOp",EDGE,"E166");Q31=makeQuery(id+"F0.imprint","IMPRINT",FACE,{"disambiguationData":[TD([[makeQuery(id+"F0.imprint","IMPRINT",EDGE,{"derivedFrom":subQ8}),1.0]])]});}
            var Q32;
            {var subQ8=sQuery(id+"F0.wireOp",EDGE,"E142");Q32=makeQuery(id+"F0.imprint","IMPRINT",FACE,{"disambiguationData":[TD([[makeQuery(id+"F0.imprint","IMPRINT",EDGE,{"derivedFrom":subQ8}),1.0]])]});}
            var Q33;
            {var subQ8=sQuery(id+"F0.wireOp",EDGE,"E154");Q33=makeQuery(id+"F0.imprint","IMPRINT",FACE,{"disambiguationData":[TD([[makeQuery(id+"F0.imprint","IMPRINT",EDGE,{"derivedFrom":subQ8}),1.0]])]});}
            var Q34;
            {var subQ5=sQuery(id+"F0.wireOp",EDGE,"E130");Q34=makeQuery(id+"F0.imprint","IMPRINT",FACE,{"disambiguationData":[TD([[makeQuery(id+"F0.imprint","IMPRINT",EDGE,{"derivedFrom":subQ5}),1.0]])]});}
            var Q35;
            {var subQ8=sQuery(id+"F0.wireOp",EDGE,"E118");Q35=makeQuery(id+"F0.imprint","IMPRINT",FACE,{"disambiguationData":[TD([[makeQuery(id+"F0.imprint","IMPRINT",EDGE,{"derivedFrom":subQ8}),1.0]])]});}
            var Q36;
            {var subQ5=sQuery(id+"F0.wireOp",EDGE,"E106");Q36=makeQuery(id+"F0.imprint","IMPRINT",FACE,{"disambiguationData":[TD([[makeQuery(id+"F0.imprint","IMPRINT",EDGE,{"derivedFrom":subQ5}),1.0]])]});}
            var Q37;
            {var subQ5=sQuery(id+"F0.wireOp",EDGE,"E9");Q37=makeQuery(id+"F0.imprint","IMPRINT",FACE,{"disambiguationData":[TD([[makeQuery(id+"F0.imprint","IMPRINT",EDGE,{"derivedFrom":subQ5}),1.0]])]});}
            var Q38;
            Q38=makeQuery(id+"F0.imprint","IMPRINT",FACE,{"disambiguationData":[TD([[makeQuery(id+"F0.imprint","IMPRINT",EDGE,{"derivedFrom":sQuery(id+"F0.wireOp",EDGE,"E285")}),1.0]])]});
            var Q39;
            Q39=makeQuery(id+"F0.imprint","IMPRINT",FACE,{"disambiguationData":[TD([[makeQuery(id+"F0.imprint","IMPRINT",EDGE,{"derivedFrom":sQuery(id+"F0.wireOp",EDGE,"E177")}),1.0]])]});
            var Q40;
            Q40=makeQuery(id+"F0.imprint","IMPRINT",FACE,{"disambiguationData":[TD([[makeQuery(id+"F0.imprint","IMPRINT",EDGE,{"derivedFrom":sQuery(id+"F0.wireOp",EDGE,"E281")}),1.0]])]});
            var Q41;
            {var subQ5=sQuery(id+"F0.wireOp",EDGE,"E21");Q41=makeQuery(id+"F0.imprint","IMPRINT",FACE,{"disambiguationData":[TD([[makeQuery(id+"F0.imprint","IMPRINT",EDGE,{"derivedFrom":subQ5}),1.0]])]});}
            extrude(context, id + "F1", {"entities" : qUnion([Q0, Q1, Q2, Q3, Q4, Q5, Q6, Q7, Q8, Q9, Q10, Q11, Q12, Q13, Q14, Q15, Q16, Q17, Q18, Q19, Q20, Q21, Q22, Q23, Q24, Q25, Q26, Q27, Q28, Q29, Q30, Q31, Q32, Q33, Q34, Q35, Q36, Q37, Q38, Q39, Q40, Q41]), "depth" : 1 * mm, "offsetDistance" : 25 * mm});
        }
    });
